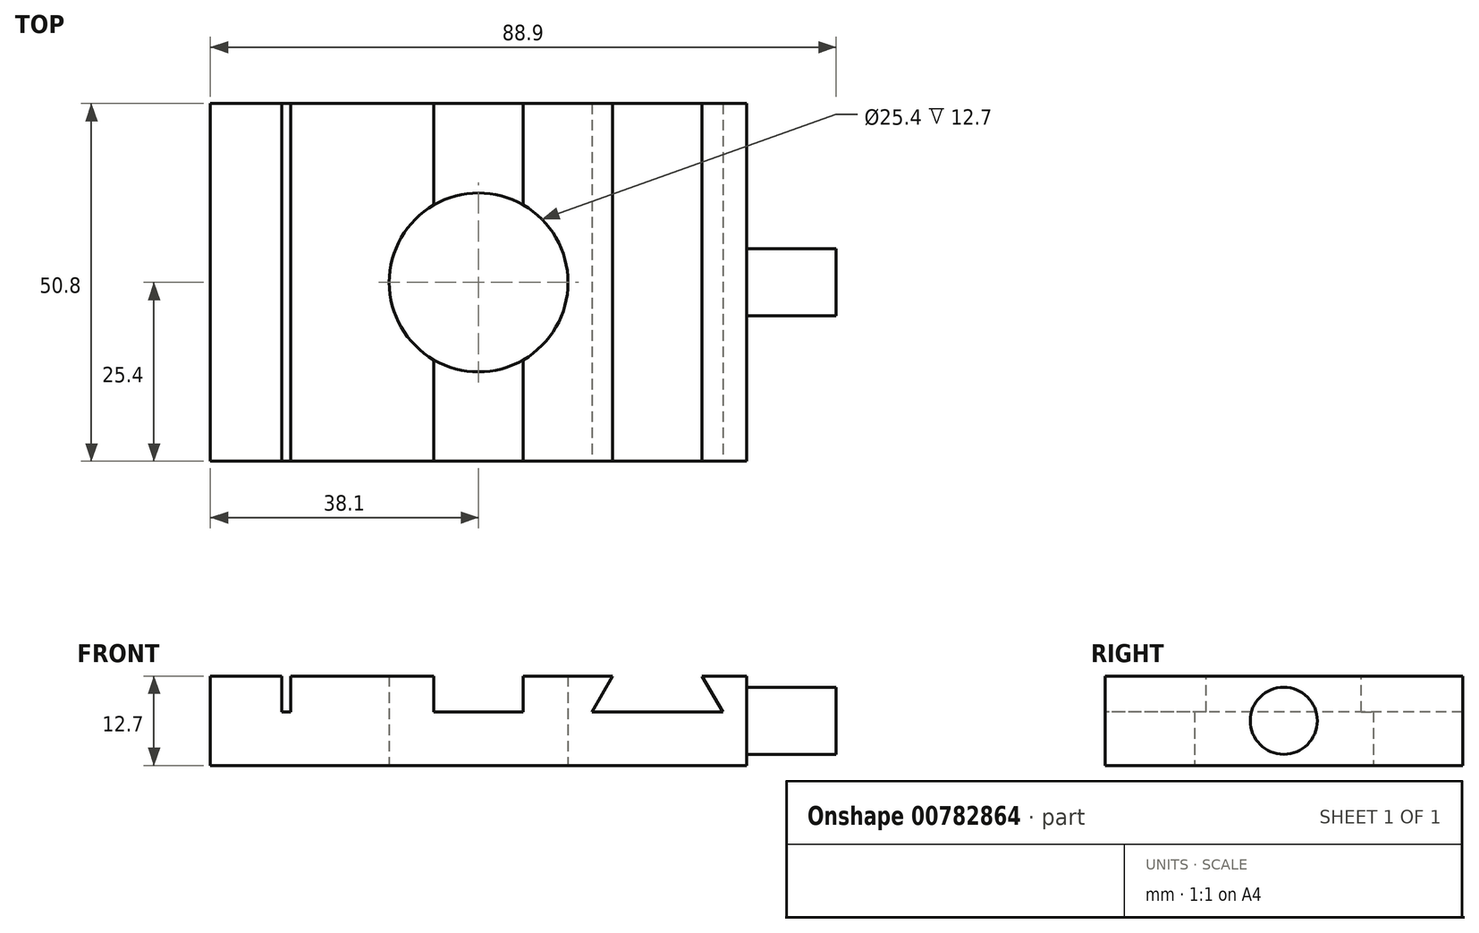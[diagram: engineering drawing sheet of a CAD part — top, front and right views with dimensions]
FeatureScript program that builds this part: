
annotation { "Feature Type Name" : "Feature", "Feature Type Description" : "" }
export const myFeature = defineFeature(function(context is Context, id is Id, definition is map)
    precondition{}
    {
        {
            var Q0;
            Q0=qCreatedBy(makeId("Top.planeOp"),FACE);
            var sketch = newSketch(context, id + "F0", { "sketchPlane" : qUnion([Q0])});
            skLineSegment(sketch, "E0.bottom", {"start": v(38.1, 25.4) * mm, "end": v(-38.1, 25.4) * mm});
            skLineSegment(sketch, "E0.top", {"start": v(38.1, -25.4) * mm, "end": v(-38.1, -25.4) * mm});
            skLineSegment(sketch, "E0.left", {"start": v(38.1, 25.4) * mm, "end": v(38.1, -25.4) * mm});
            skLineSegment(sketch, "E0.right", {"start": v(-38.1, 25.4) * mm, "end": v(-38.1, -25.4) * mm});
            skPoint(sketch, "E0.middle", {"position": v(0, 0) * mm});
            skCircle(sketch, "E1", {"center": v(0, 0) * mm, "radius": 12.7 * mm});
            skSolve(sketch);
        }
        {
            var Q0;
            Q0=makeQuery(id+"F0.imprint","IMPRINT",FACE,{"disambiguationData":[TD([[makeQuery(id+"F0.imprint","IMPRINT",EDGE,{"derivedFrom":sQuery(id+"F0.wireOp",EDGE,"E0.bottom")}),1.0]])]});
            extrude(context, id + "F1", {"entities" : qUnion([Q0]), "depth" : 12.7 * mm, "offsetDistance" : 25.4 * mm});
        }
        {
            var Q0;
            Q0=makeQuery(id+"F1.opExtrude","CAP_FACE",FACE,{"disambiguationData":[OSD([sQuery(id+"F0.wireOp",EDGE,"E0.bottom"),sQuery(id+"F0.wireOp",EDGE,"E0.top"),sQuery(id+"F0.wireOp",EDGE,"E0.left"),sQuery(id+"F0.wireOp",EDGE,"E0.right"),sQuery(id+"F0.wireOp",EDGE,"E1")])],"isStart":false});
            var sketch = newSketch(context, id + "F2", { "sketchPlane" : qUnion([Q0])});
            skLineSegment(sketch, "E2.bottom", {"start": v(-27.94, 25.4) * mm, "end": v(-26.67, 25.4) * mm});
            skLineSegment(sketch, "E2.top", {"start": v(-27.94, -25.4) * mm, "end": v(-26.67, -25.4) * mm});
            skLineSegment(sketch, "E2.left", {"start": v(-27.94, 25.4) * mm, "end": v(-27.94, -25.4) * mm});
            skLineSegment(sketch, "E2.right", {"start": v(-26.67, 25.4) * mm, "end": v(-26.67, -25.4) * mm});
            skLineSegment(sketch, "E3", {"start": v(-6.35, 25.4) * mm, "end": v(-6.35, -25.4) * mm});
            skLineSegment(sketch, "E4", {"start": v(-6.35, -25.4) * mm, "end": v(6.35, -25.4) * mm});
            skLineSegment(sketch, "E5", {"start": v(6.35, -25.4) * mm, "end": v(6.35, 25.4) * mm});
            skPoint(sketch, "E6", {"position": v(0, 0) * mm});
            skLineSegment(sketch, "E7", {"start": v(0, -25.4) * mm, "end": v(0, 25.4) * mm, "construction": true});
            skSolve(sketch);
        }
        {
            var Q0;
            Q0=makeQuery(id+"F2.imprint","IMPRINT",FACE,{"disambiguationData":[TD([[makeQuery(id+"F2.imprint","IMPRINT",EDGE,{"derivedFrom":sQuery(id+"F2.wireOp",EDGE,"E2.bottom")}),1.0]])]});
            var Q1;
            {var subQ0=sQuery(id+"F2.wireOp",EDGE,"E3");var subQ1=makeQuery(id+"F1.opExtrude","CAP_EDGE",EDGE,{"disambiguationData":[OSD([sQuery(id+"F0.wireOp",EDGE,"E0.bottom")])],"isStart":false});var subQ2=makeQuery(id+"F2.imprint","INTERSECT",VERTEX,{"derivedFrom":[subQ1,subQ0]});Q1=makeQuery(id+"F2.imprint","IMPRINT",FACE,{"disambiguationData":[TD([[makeQuery(id+"F2.imprint","IMPRINT",EDGE,{"disambiguationData":[TD([[subQ2,-1.0]])],"derivedFrom":subQ0}),1.0]])]});}
            var Q2;
            {var subQ0=sQuery(id+"F2.wireOp",EDGE,"E4");Q2=makeQuery(id+"F2.imprint","IMPRINT",FACE,{"disambiguationData":[TD([[makeQuery(id+"F2.imprint","IMPRINT",EDGE,{"derivedFrom":subQ0}),-1.0]])]});}
            extrude(context, id + "F3", {"entities" : qUnion([Q0, Q1, Q2]), "operationType" : NewBodyOperationType.REMOVE, "oppositeDirection" : true, "depth" : 5.08 * mm, "offsetDistance" : 25.4 * mm});
        }
        {
            var Q0;
            Q0=makeQuery(id+"F1.opExtrude","SWEPT_FACE",FACE,{"disambiguationData":[OSD([sQuery(id+"F0.wireOp",EDGE,"E0.top")])]});
            var sketch = newSketch(context, id + "F4", { "sketchPlane" : qUnion([Q0])});
            skLineSegment(sketch, "E8", {"start": v(19.05, 12.7) * mm, "end": v(16.12, 7.62) * mm});
            skLineSegment(sketch, "E9", {"start": v(16.12, 7.62) * mm, "end": v(34.68, 7.62) * mm});
            skLineSegment(sketch, "E10", {"start": v(34.68, 7.62) * mm, "end": v(31.75, 12.7) * mm});
            skLineSegment(sketch, "E11", {"start": v(31.75, 12.7) * mm, "end": v(19.05, 12.7) * mm});
            skLineSegment(sketch, "E12", {"start": v(25.4, 7.62) * mm, "end": v(25.4, 12.7) * mm, "construction": true});
            skSolve(sketch);
        }
        {
            var Q0;
            Q0=makeQuery(id+"F4.imprint","IMPRINT",FACE,{"disambiguationData":[TD([[makeQuery(id+"F4.imprint","IMPRINT",EDGE,{"derivedFrom":sQuery(id+"F4.wireOp",EDGE,"E8")}),1.0]])]});
            extrude(context, id + "F5", {"entities" : qUnion([Q0]), "operationType" : NewBodyOperationType.REMOVE, "endBound" : BoundingType.THROUGH_ALL, "oppositeDirection" : true, "depth" : 18.03 * mm, "offsetDistance" : 25.4 * mm});
        }
        {
            var Q0;
            Q0=makeQuery(id+"F1.opExtrude","SWEPT_FACE",FACE,{"disambiguationData":[OSD([sQuery(id+"F0.wireOp",EDGE,"E0.left")])]});
            var sketch = newSketch(context, id + "F6", { "sketchPlane" : qUnion([Q0])});
            skCircle(sketch, "E13", {"center": v(0, 6.35) * mm, "radius": 4.76 * mm});
            skPoint(sketch, "E13.centerSnap0", {"position": v(-25.4, 6.35) * mm});
            skPoint(sketch, "E13.centerSnap1", {"position": v(0, 12.7) * mm});
            skSolve(sketch);
        }
        {
            var Q0;
            Q0=makeQuery(id+"F6.imprint","IMPRINT",FACE,{"disambiguationData":[TD([[makeQuery(id+"F6.imprint","IMPRINT",EDGE,{"derivedFrom":sQuery(id+"F6.wireOp",EDGE,"E13")}),1.0]])]});
            extrude(context, id + "F7", {"entities" : qUnion([Q0]), "operationType" : NewBodyOperationType.ADD, "depth" : 12.7 * mm, "offsetDistance" : 25.4 * mm});
        }
    });
